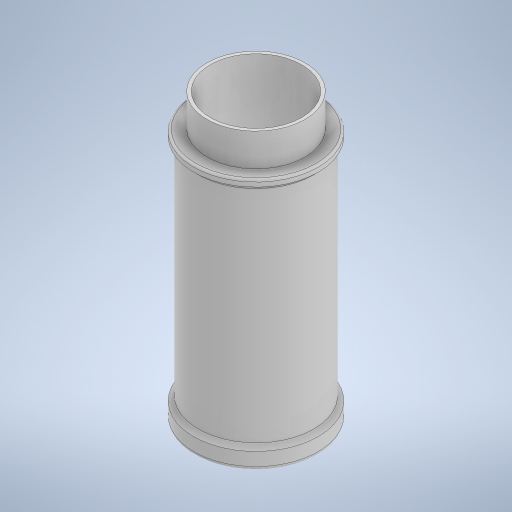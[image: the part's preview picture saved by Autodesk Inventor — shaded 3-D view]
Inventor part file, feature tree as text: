
AUTODESK INVENTOR PART (.ipt)
format: ipt  version: 2023 (Build 270158000, 158)  size: 290,816 bytes
history: native  units: in
note: dims shown in document units (in); Inventor stores cm internally (conversion verified against a paired STEP export)
features: sketch x5, extrude x3, chamfer x2, fillet x2, plane x1, revolve x1
ambient origin geometry x8: Origin, YZ Plane, XZ Plane, XY Plane, X Axis, Y Axis, Z Axis, Center Point
bodies: Solid1 (feature_tree)
feature tree (14):
  extrude  "Extrusion1"  Depth=5.1575in TaperAngle=0.0deg
  extrude  "Extrusion2"  Depth=1.7717in
  plane  "Work Plane2"
  revolve  "Revolution1"  [1 undecoded]
  chamfer  "Chamfer1"  Distance=0.0787in
  chamfer  "Chamfer2"  Distance=0.3937in
  fillet  "Fillet1"  Radius=0.0787in
  fillet  "Fillet2"  [1 undecoded]
  sketch  "Sketch5"  dims[d8=2.2441in]
  extrude  "Extrusion3"  Depth=0.0787in TaperAngle=45.0deg
  sketch  "Sketch1"  dims[d0=2.2441in d1=5.1575in d2=0.0in]
  sketch  "Sketch2"  dims[d3=1.9685in d4=1.7717in]
  sketch  "Sketch4"  dims[d5=0.5906in d6=0.0in d7=0.0in]
  sketch  "Sketch6"  dims[d10=0.1969in d11=0.0787in d12=0.3937in d13=0.0787in d14=90.0deg d15=0.0787in d16=0.0787in d17=45.0deg d18=0.0787in d19=0.0787in d20=45.0deg d21=0.0787in d22=0.0394in d27=1.6535in d28=4.9213in d29=0.0in]
note: 2 required parameter values undecoded (feature->parameter linkage not recoverable at this tier; creation-order binding heuristic only, values carry confidence <= 0.55)